# Revit family: 351_f2b97774768d49cb8b3b618e5e86cf
name_source: partatom
category: Plumbing Fixtures
units: mm (PartAtom-declared; Revit-internal decimal feet)

## family parameters
Always vertical = Yes
Cut with Voids When Loaded = No
Part Type = Normal
Room Calculation Point = No
Round Connector Dimension = Use Diameter
Shared = No
Work Plane-Based = No

## types (1)
- 5650156 IDO GLOW
    CARM = No
    CAT0 = Yes
    CLBTZ = 0 mm  [stored 0 ft]
    CL_Location_5000 = 5000 mm  [stored 16.4042 ft]
    D = 110 mm
    Description = WC IDO Glow 63, no screw holes, soft seat, single flush
    Manufacturer = IDO
    QmdConnectorList = 601;D
    R = 55 mm  [stored 0.180446 ft]
    R1 = 56 mm  [stored 0.183727 ft]
    SEWL = No
    SEWR = No
    URL = http://www.ido.fi
    XRefLineVPlnId = 7453
    YRefLineVPlnId = 7456
    magiPartTypeId = 351
    magiProductCode = 5650156 IDO GLOW
    magiProductFamilyId = f2b97774768d49cb8b3b618e5e86cf
    magiProductId = f2b97774768d49cb8b3b618e5e86cf

note: [stored X ft] marks values corroborated as IEEE doubles in the binary element streams (Revit-internal decimal feet)

## geometry (parser evidence)
native form markers: Sweep x3
no freeform markers — native parametric forms only
